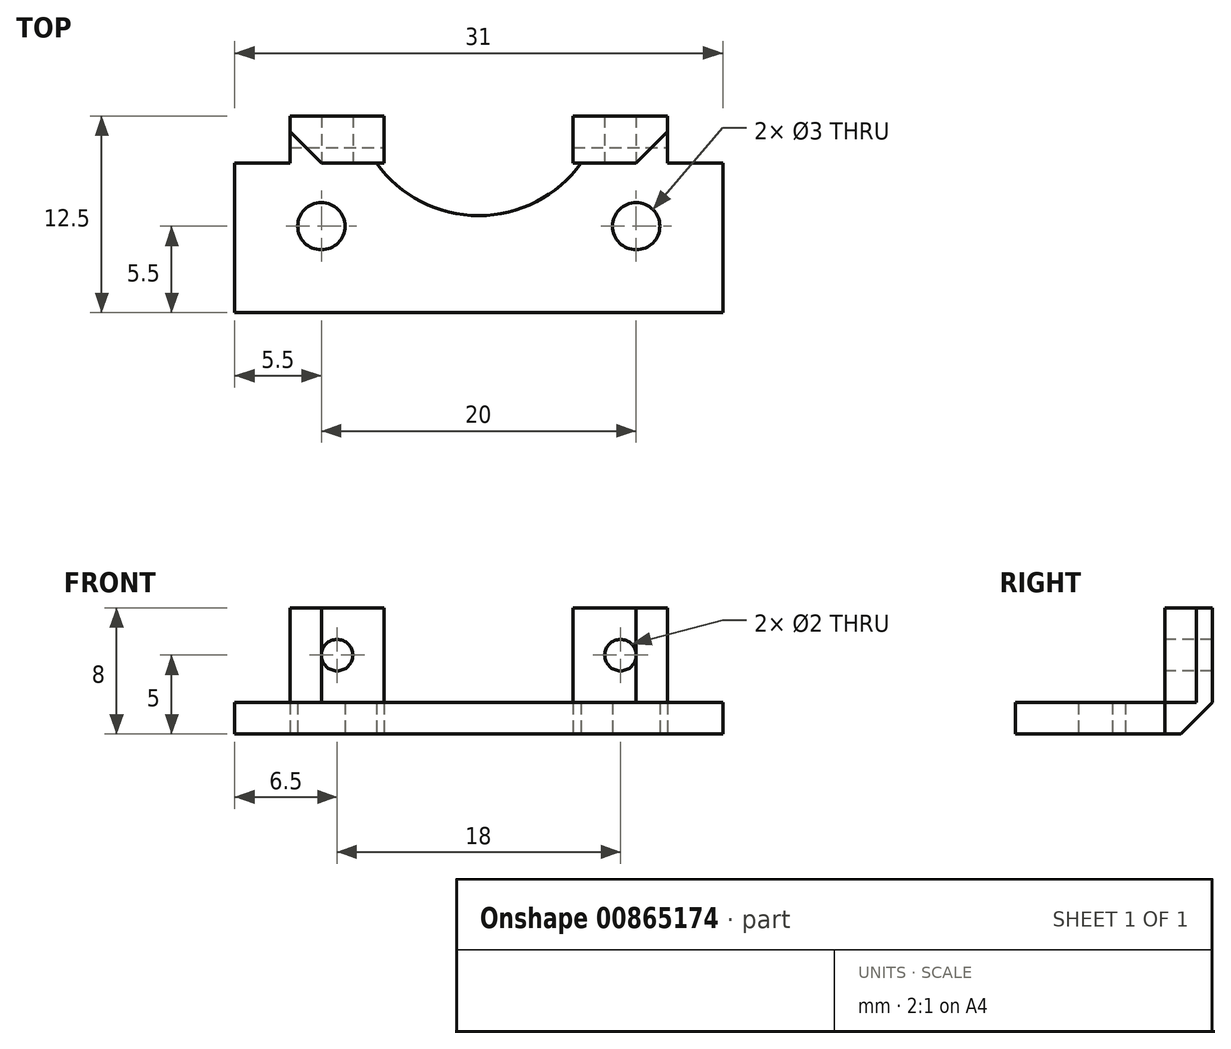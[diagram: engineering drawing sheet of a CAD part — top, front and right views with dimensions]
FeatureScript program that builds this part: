
annotation { "Feature Type Name" : "Feature", "Feature Type Description" : "" }
export const myFeature = defineFeature(function(context is Context, id is Id, definition is map)
    precondition{}
    {
        {
            var Q0;
            Q0=qCreatedBy(makeId("Top.planeOp"),FACE);
            var sketch = newSketch(context, id + "F0", { "sketchPlane" : qUnion([Q0])});
            skLineSegment(sketch, "E0.bottom", {"start": v(-15.5, 0) * mm, "end": v(15.5, 0) * mm});
            skLineSegment(sketch, "E0.top", {"start": v(-15.5, -9.5) * mm, "end": v(15.5, -9.5) * mm});
            skLineSegment(sketch, "E0.left", {"start": v(-15.5, 0) * mm, "end": v(-15.5, -9.5) * mm});
            skLineSegment(sketch, "E0.right", {"start": v(15.5, 0) * mm, "end": v(15.5, -9.5) * mm});
            skCircle(sketch, "E1", {"center": v(-10, -4) * mm, "radius": 1.5 * mm});
            skCircle(sketch, "E2", {"center": v(10, -4) * mm, "radius": 1.5 * mm});
            skLineSegment(sketch, "E3", {"start": v(-10, -4) * mm, "end": v(10, -4) * mm, "construction": true});
            skArc(sketch, "E4", {"start": v(-6.5, 0) * mm, "mid": v(0, -3.34) * mm, "end": v(6.5, 0) * mm});
            skSolve(sketch);
        }
        {
            var Q0;
            Q0=makeQuery(id+"F0.imprint","IMPRINT",FACE,{"disambiguationData":[TD([[makeQuery(id+"F0.imprint","IMPRINT",EDGE,{"derivedFrom":sQuery(id+"F0.wireOp",EDGE,"E0.top")}),1.0]])]});
            extrude(context, id + "F1", {"entities" : qUnion([Q0]), "depth" : 2 * mm, "offsetDistance" : 25 * mm});
        }
        {
            var Q0;
            Q0=qCreatedBy(makeId("Front.planeOp"),FACE);
            var sketch = newSketch(context, id + "F2", { "sketchPlane" : qUnion([Q0])});
            skCircle(sketch, "E5", {"center": v(-9, 5) * mm, "radius": 1 * mm});
            skCircle(sketch, "E6", {"center": v(9, 5) * mm, "radius": 1 * mm});
            skLineSegment(sketch, "E7", {"start": v(-9, 5) * mm, "end": v(9, 5) * mm, "construction": true});
            skLineSegment(sketch, "E8.bottom", {"start": v(-12, 8) * mm, "end": v(-6, 8) * mm});
            skLineSegment(sketch, "E8.top", {"start": v(-12, 0) * mm, "end": v(-6, 0) * mm});
            skLineSegment(sketch, "E8.left", {"start": v(-12, 8) * mm, "end": v(-12, 0) * mm});
            skLineSegment(sketch, "E8.right", {"start": v(-6, 8) * mm, "end": v(-6, 0) * mm});
            skLineSegment(sketch, "E9.bottom", {"start": v(6, 8) * mm, "end": v(12, 8) * mm});
            skLineSegment(sketch, "E9.top", {"start": v(6, 0) * mm, "end": v(12, 0) * mm});
            skLineSegment(sketch, "E9.left", {"start": v(6, 8) * mm, "end": v(6, 0) * mm});
            skLineSegment(sketch, "E9.right", {"start": v(12, 8) * mm, "end": v(12, 0) * mm});
            skLineSegment(sketch, "E10", {"start": v(-9, 8) * mm, "end": v(-9, 0) * mm, "construction": true});
            skLineSegment(sketch, "E11", {"start": v(9, 8) * mm, "end": v(9, 0) * mm, "construction": true});
            skLineSegment(sketch, "E12", {"start": v(6, 0) * mm, "end": v(-6, 0) * mm, "construction": true});
            skSolve(sketch);
        }
        {
            var Q0;
            Q0 = qSketchRegion(id + "F2", true);
            extrude(context, id + "F3", {"entities" : qUnion([Q0]), "operationType" : NewBodyOperationType.ADD, "oppositeDirection" : true, "depth" : 3 * mm, "offsetDistance" : 25 * mm});
        }
        {
            var Q0;
            Q0=makeQuery(id+"F3.opExtrude","CAP_EDGE",EDGE,{"disambiguationData":[OSD([sQuery(id+"F2.wireOp",EDGE,"E9.top")])],"isStart":false});
            var Q1;
            Q1=makeQuery(id+"F3.opExtrude","CAP_EDGE",EDGE,{"disambiguationData":[OSD([sQuery(id+"F2.wireOp",EDGE,"E8.top")])],"isStart":false});
            chamfer(context, id + "F4", {"entities" : qUnion([Q0, Q1]), "width" : 2 * mm, "tangentPropagation" : true});
        }
        {
            var Q0;
            {var subQ0=sQuery(id+"F0.wireOp",EDGE,"E0.bottom");var subQ1=sQuery(id+"F2.wireOp",EDGE,"E9.right");Q0=makeQuery(id+"F3.boolean.opBoolean","SPLIT",EDGE,{"disambiguationData":[topologyDisambiguationEdgeConnected([makeQuery(id+"F1.opExtrude","SWEPT_FACE",FACE,{"disambiguationData":[OSD([subQ0]),TDD([makeQuery(id+"F0.imprint","IMPRINT",EDGE,{"disambiguationData":[TD([[makeQuery(id+"F0.imprint","INTERSECT",VERTEX,{"derivedFrom":[subQ0,sQuery(id+"F0.wireOp",EDGE,"E0.right")]}),1.0]])],"derivedFrom":subQ0})])]})])],"derivedFrom":makeQuery(id+"F3.opExtrude","CAP_EDGE",EDGE,{"disambiguationData":[OSD([subQ1])],"isStart":true})});}
            var Q1;
            {var subQ0=sQuery(id+"F0.wireOp",EDGE,"E0.bottom");var subQ1=sQuery(id+"F2.wireOp",EDGE,"E8.left");Q1=makeQuery(id+"F3.boolean.opBoolean","SPLIT",EDGE,{"disambiguationData":[topologyDisambiguationEdgeConnected([makeQuery(id+"F1.opExtrude","SWEPT_FACE",FACE,{"disambiguationData":[OSD([subQ0]),TDD([makeQuery(id+"F0.imprint","IMPRINT",EDGE,{"disambiguationData":[TD([[makeQuery(id+"F0.imprint","INTERSECT",VERTEX,{"derivedFrom":[subQ0,sQuery(id+"F0.wireOp",EDGE,"E0.left")]}),-1.0]])],"derivedFrom":subQ0})])]})])],"derivedFrom":makeQuery(id+"F3.opExtrude","CAP_EDGE",EDGE,{"disambiguationData":[OSD([subQ1])],"isStart":true})});}
            chamfer(context, id + "F5", {"entities" : qUnion([Q0, Q1]), "width" : 2 * mm});
        }
    });
